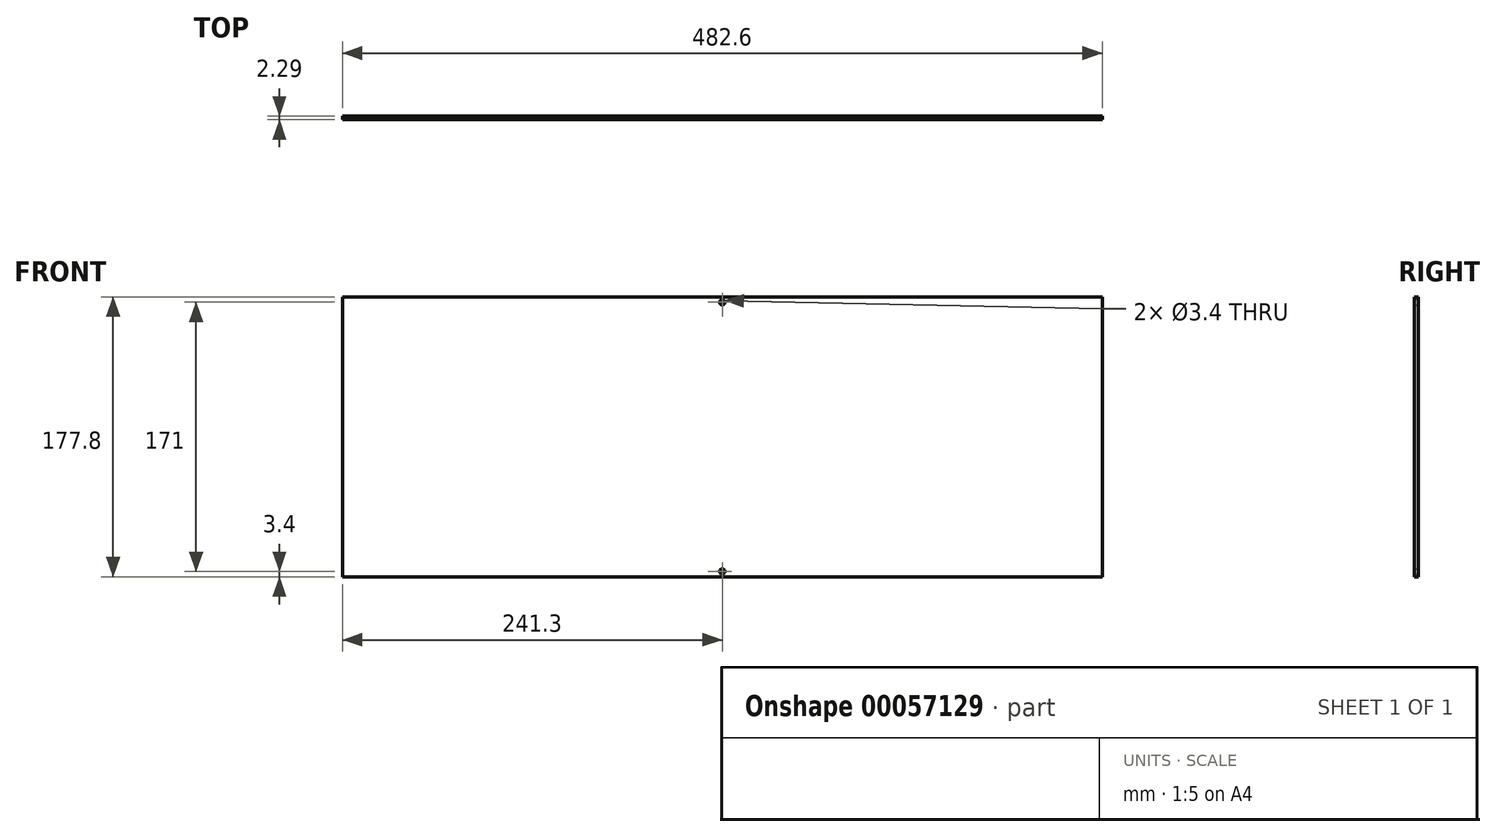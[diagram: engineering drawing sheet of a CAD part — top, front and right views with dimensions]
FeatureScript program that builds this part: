
annotation { "Feature Type Name" : "Feature", "Feature Type Description" : "" }
export const myFeature = defineFeature(function(context is Context, id is Id, definition is map)
    precondition{}
    {
        {
            var Q0;
            Q0=qCreatedBy(makeId("Front.planeOp"),FACE);
            var sketch = newSketch(context, id + "F0", { "sketchPlane" : qUnion([Q0])});
            skLineSegment(sketch, "E0.rect.bottom", {"start": v(241.3, 88.9) * mm, "end": v(-241.3, 88.9) * mm});
            skLineSegment(sketch, "E0.rect.top", {"start": v(241.3, -88.9) * mm, "end": v(-241.3, -88.9) * mm});
            skLineSegment(sketch, "E0.rect.left", {"start": v(241.3, 88.9) * mm, "end": v(241.3, -88.9) * mm});
            skLineSegment(sketch, "E0.rect.right", {"start": v(-241.3, 88.9) * mm, "end": v(-241.3, -88.9) * mm});
            skPoint(sketch, "E0.rect.middle", {"position": v(0, 0) * mm});
            skLineSegment(sketch, "E1", {"start": v(0, 88.9) * mm, "end": v(0, -88.9) * mm, "construction": true});
            skCircle(sketch, "E2", {"center": v(0, 85.5) * mm, "radius": 1.7 * mm});
            skCircle(sketch, "E3.MirrorC", {"center": v(0, -85.5) * mm, "radius": 1.7 * mm});
            skLineSegment(sketch, "E4", {"start": v(-241.3, 85.5) * mm, "end": v(241.3, 85.5) * mm, "construction": true});
            skSolve(sketch);
        }
        {
            var Q0;
            Q0=makeQuery(id+"F0.imprint","IMPRINT",FACE,{"disambiguationData":[TD([[makeQuery(id+"F0.imprint","IMPRINT",EDGE,{"derivedFrom":sQuery(id+"F0.wireOp",EDGE,"E0.rect.bottom")}),1.0]])]});
            extrude(context, id + "F1", {"entities" : qUnion([Q0]), "depth" : 2.3 * mm});
        }
    });
